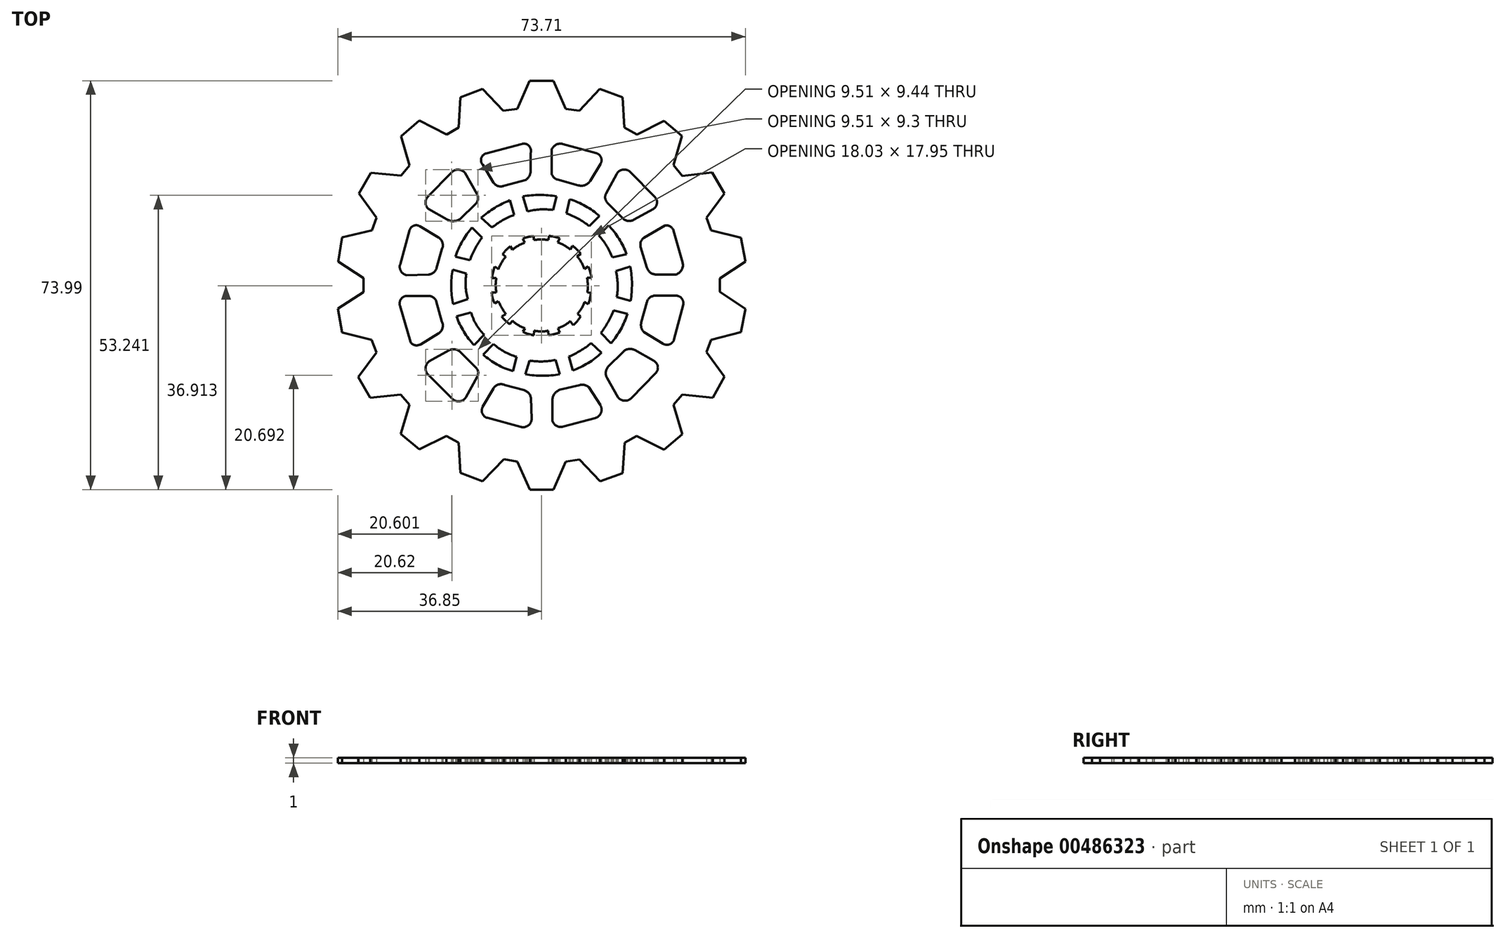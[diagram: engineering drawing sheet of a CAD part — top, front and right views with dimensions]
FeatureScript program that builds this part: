
annotation { "Feature Type Name" : "Feature", "Feature Type Description" : "" }
export const myFeature = defineFeature(function(context is Context, id is Id, definition is map)
    precondition{}
    {
        {
            var Q0;
            Q0=qCreatedBy(makeId("Top.planeOp"),FACE);
            var sketch = newSketch(context, id + "F0", { "sketchPlane" : qUnion([Q0])});
            skLineSegment(sketch, "E0", {"start": v(-17.03, 27.3) * mm, "end": v(-14.85, 28.54) * mm});
            skLineSegment(sketch, "E1", {"start": v(-14.85, 28.54) * mm, "end": v(-14.52, 34.02) * mm});
            skLineSegment(sketch, "E2", {"start": v(-14.52, 34.02) * mm, "end": v(-10.54, 35.55) * mm});
            skLineSegment(sketch, "E3", {"start": v(-10.54, 35.55) * mm, "end": v(-6.75, 31.57) * mm});
            skLineSegment(sketch, "E4", {"start": v(-6.75, 31.57) * mm, "end": v(-4.21, 31.95) * mm});
            skLineSegment(sketch, "E5", {"start": v(-4.21, 31.95) * mm, "end": v(-2.01, 37.02) * mm});
            skLineSegment(sketch, "E6", {"start": v(-2.01, 37.02) * mm, "end": v(2.27, 37.02) * mm});
            skLineSegment(sketch, "E7", {"start": v(2.27, 37.02) * mm, "end": v(4.5, 31.95) * mm});
            skLineSegment(sketch, "E8", {"start": v(4.5, 31.95) * mm, "end": v(7, 31.57) * mm});
            skLineSegment(sketch, "E9", {"start": v(7, 31.57) * mm, "end": v(10.7, 35.55) * mm});
            skLineSegment(sketch, "E10", {"start": v(10.7, 35.55) * mm, "end": v(14.82, 34.02) * mm});
            skLineSegment(sketch, "E11", {"start": v(14.82, 34.02) * mm, "end": v(15.12, 28.54) * mm});
            skLineSegment(sketch, "E12", {"start": v(15.12, 28.54) * mm, "end": v(17.42, 27.3) * mm});
            skLineSegment(sketch, "E13", {"start": v(17.42, 27.3) * mm, "end": v(22.3, 29.76) * mm});
            skLineSegment(sketch, "E14", {"start": v(22.3, 29.76) * mm, "end": v(25.55, 27.03) * mm});
            skLineSegment(sketch, "E15", {"start": v(25.55, 27.03) * mm, "end": v(24.01, 21.74) * mm});
            skLineSegment(sketch, "E16", {"start": v(24.01, 21.74) * mm, "end": v(25.62, 19.8) * mm});
            skLineSegment(sketch, "E17", {"start": v(25.62, 19.8) * mm, "end": v(31.02, 20.4) * mm});
            skLineSegment(sketch, "E18", {"start": v(31.02, 20.4) * mm, "end": v(33.2, 16.62) * mm});
            skLineSegment(sketch, "E19", {"start": v(33.2, 16.62) * mm, "end": v(30.01, 12.24) * mm});
            skLineSegment(sketch, "E20", {"start": v(30.01, 12.24) * mm, "end": v(30.84, 9.94) * mm});
            skLineSegment(sketch, "E21", {"start": v(30.84, 9.94) * mm, "end": v(36.21, 8.6) * mm});
            skLineSegment(sketch, "E22", {"start": v(36.21, 8.6) * mm, "end": v(37.02, 4.26) * mm});
            skLineSegment(sketch, "E23", {"start": v(37.02, 4.26) * mm, "end": v(32.38, 1.27) * mm});
            skLineSegment(sketch, "E24", {"start": v(32.38, 1.27) * mm, "end": v(32.38, -1.18) * mm});
            skLineSegment(sketch, "E25", {"start": v(32.38, -1.18) * mm, "end": v(37.02, -4.3) * mm});
            skLineSegment(sketch, "E26", {"start": v(37.02, -4.3) * mm, "end": v(36.23, -8.5) * mm});
            skLineSegment(sketch, "E27", {"start": v(36.23, -8.5) * mm, "end": v(30.81, -9.85) * mm});
            skLineSegment(sketch, "E28", {"start": v(30.81, -9.85) * mm, "end": v(29.96, -12.09) * mm});
            skLineSegment(sketch, "E29", {"start": v(29.96, -12.09) * mm, "end": v(33.2, -16.56) * mm});
            skLineSegment(sketch, "E30", {"start": v(33.2, -16.56) * mm, "end": v(31.11, -20.31) * mm});
            skLineSegment(sketch, "E31", {"start": v(31.11, -20.31) * mm, "end": v(25.59, -19.74) * mm});
            skLineSegment(sketch, "E32", {"start": v(25.59, -19.74) * mm, "end": v(24.04, -21.63) * mm});
            skLineSegment(sketch, "E33", {"start": v(24.04, -21.63) * mm, "end": v(25.58, -26.96) * mm});
            skLineSegment(sketch, "E34", {"start": v(25.58, -26.96) * mm, "end": v(22.31, -29.71) * mm});
            skLineSegment(sketch, "E35", {"start": v(22.31, -29.71) * mm, "end": v(17.32, -27.25) * mm});
            skLineSegment(sketch, "E36", {"start": v(17.32, -27.25) * mm, "end": v(15.17, -28.48) * mm});
            skLineSegment(sketch, "E37", {"start": v(15.17, -28.48) * mm, "end": v(14.84, -34.01) * mm});
            skLineSegment(sketch, "E38", {"start": v(14.84, -34.01) * mm, "end": v(10.72, -35.46) * mm});
            skLineSegment(sketch, "E39", {"start": v(10.72, -35.46) * mm, "end": v(6.97, -31.5) * mm});
            skLineSegment(sketch, "E40", {"start": v(6.97, -31.5) * mm, "end": v(4.53, -31.92) * mm});
            skLineSegment(sketch, "E41", {"start": v(4.53, -31.92) * mm, "end": v(2.3, -36.97) * mm});
            skLineSegment(sketch, "E42", {"start": v(2.3, -36.97) * mm, "end": v(-1.97, -36.97) * mm});
            skLineSegment(sketch, "E43", {"start": v(-1.97, -36.97) * mm, "end": v(-4.23, -31.92) * mm});
            skLineSegment(sketch, "E44", {"start": v(-4.23, -31.92) * mm, "end": v(-6.66, -31.48) * mm});
            skLineSegment(sketch, "E45", {"start": v(-6.66, -31.48) * mm, "end": v(-10.5, -35.46) * mm});
            skLineSegment(sketch, "E46", {"start": v(-10.5, -35.46) * mm, "end": v(-14.56, -33.92) * mm});
            skLineSegment(sketch, "E47", {"start": v(-14.56, -33.92) * mm, "end": v(-14.87, -28.5) * mm});
            skLineSegment(sketch, "E48", {"start": v(-14.87, -28.5) * mm, "end": v(-17.04, -27.25) * mm});
            skLineSegment(sketch, "E49", {"start": v(-17.04, -27.25) * mm, "end": v(-21.98, -29.68) * mm});
            skLineSegment(sketch, "E50", {"start": v(-21.98, -29.68) * mm, "end": v(-25.3, -26.9) * mm});
            skLineSegment(sketch, "E51", {"start": v(-25.3, -26.9) * mm, "end": v(-23.76, -21.61) * mm});
            skLineSegment(sketch, "E52", {"start": v(-23.76, -21.61) * mm, "end": v(-25.32, -19.78) * mm});
            skLineSegment(sketch, "E53", {"start": v(-25.32, -19.78) * mm, "end": v(-30.85, -20.35) * mm});
            skLineSegment(sketch, "E54", {"start": v(-30.85, -20.35) * mm, "end": v(-33, -16.6) * mm});
            skLineSegment(sketch, "E55", {"start": v(-33, -16.6) * mm, "end": v(-29.73, -12.12) * mm});
            skLineSegment(sketch, "E56", {"start": v(-29.73, -12.12) * mm, "end": v(-30.57, -9.84) * mm});
            skLineSegment(sketch, "E57", {"start": v(-30.57, -9.84) * mm, "end": v(-35.96, -8.52) * mm});
            skLineSegment(sketch, "E58", {"start": v(-35.96, -8.52) * mm, "end": v(-36.7, -4.24) * mm});
            skLineSegment(sketch, "E59", {"start": v(-36.7, -4.24) * mm, "end": v(-32.06, -1.25) * mm});
            skLineSegment(sketch, "E60", {"start": v(-32.06, -1.25) * mm, "end": v(-32.06, 1.28) * mm});
            skLineSegment(sketch, "E61", {"start": v(-32.06, 1.28) * mm, "end": v(-36.66, 4.26) * mm});
            skLineSegment(sketch, "E62", {"start": v(-36.66, 4.26) * mm, "end": v(-35.9, 8.67) * mm});
            skLineSegment(sketch, "E63", {"start": v(-35.9, 8.67) * mm, "end": v(-30.55, 9.94) * mm});
            skLineSegment(sketch, "E64", {"start": v(-30.55, 9.94) * mm, "end": v(-29.69, 12.2) * mm});
            skLineSegment(sketch, "E65", {"start": v(-29.69, 12.2) * mm, "end": v(-32.88, 16.62) * mm});
            skLineSegment(sketch, "E66", {"start": v(-32.88, 16.62) * mm, "end": v(-30.75, 20.39) * mm});
            skLineSegment(sketch, "E67", {"start": v(-30.75, 20.39) * mm, "end": v(-25.28, 19.83) * mm});
            skLineSegment(sketch, "E68", {"start": v(-25.28, 19.83) * mm, "end": v(-23.75, 21.7) * mm});
            skLineSegment(sketch, "E69", {"start": v(-23.75, 21.7) * mm, "end": v(-25.28, 27) * mm});
            skLineSegment(sketch, "E70", {"start": v(-25.28, 27) * mm, "end": v(-21.98, 29.8) * mm});
            skLineSegment(sketch, "E71", {"start": v(-21.98, 29.8) * mm, "end": v(-17.03, 27.3) * mm});
            skLineSegment(sketch, "E72", {"start": v(-21.88, 10.7) * mm, "end": v(-18.54, 8.69) * mm});
            skArc(sketch, "E73", {"start": v(-17.87, 6.53) * mm, "mid": v(-17.79, 7.74) * mm, "end": v(-18.54, 8.69) * mm});
            skLineSegment(sketch, "E74", {"start": v(-17.87, 6.53) * mm, "end": v(-18.83, 3.16) * mm});
            skArc(sketch, "E75", {"start": v(-20.28, 1.94) * mm, "mid": v(-19.37, 2.33) * mm, "end": v(-18.83, 3.16) * mm});
            skLineSegment(sketch, "E76", {"start": v(-20.28, 1.94) * mm, "end": v(-24.3, 1.85) * mm});
            skArc(sketch, "E77", {"start": v(-25.42, 3.86) * mm, "mid": v(-25.3, 2.6) * mm, "end": v(-24.3, 1.85) * mm});
            skLineSegment(sketch, "E78", {"start": v(-25.42, 3.86) * mm, "end": v(-23.73, 9.96) * mm});
            skArc(sketch, "E79", {"start": v(-21.88, 10.7) * mm, "mid": v(-22.99, 10.79) * mm, "end": v(-23.73, 9.96) * mm});
            skLineSegment(sketch, "E80", {"start": v(-24.2, -1.9) * mm, "end": v(-20.36, -1.9) * mm});
            skLineSegment(sketch, "E81", {"start": v(-25.48, -3.7) * mm, "end": v(-23.58, -10.27) * mm});
            skLineSegment(sketch, "E82", {"start": v(-21.73, -10.67) * mm, "end": v(-18.53, -8.75) * mm});
            skLineSegment(sketch, "E83", {"start": v(-18.9, -2.9) * mm, "end": v(-17.87, -6.57) * mm});
            skArc(sketch, "E84", {"start": v(-24.2, -1.9) * mm, "mid": v(-25.28, -2.5) * mm, "end": v(-25.48, -3.7) * mm});
            skArc(sketch, "E85", {"start": v(-23.58, -10.27) * mm, "mid": v(-22.73, -10.84) * mm, "end": v(-21.73, -10.67) * mm});
            skArc(sketch, "E86", {"start": v(-18.53, -8.75) * mm, "mid": v(-17.78, -7.79) * mm, "end": v(-17.87, -6.57) * mm});
            skArc(sketch, "E87", {"start": v(-18.9, -2.9) * mm, "mid": v(-19.47, -2.18) * mm, "end": v(-20.36, -1.9) * mm});
            skLineSegment(sketch, "E88", {"start": v(-14.6, -12.01) * mm, "end": v(-11.87, -14.75) * mm});
            skLineSegment(sketch, "E89", {"start": v(-16.64, -11.78) * mm, "end": v(-20.2, -13.77) * mm});
            skLineSegment(sketch, "E90", {"start": v(-20.34, -16.22) * mm, "end": v(-15.91, -20.58) * mm});
            skLineSegment(sketch, "E91", {"start": v(-11.48, -16.52) * mm, "end": v(-13.5, -20.2) * mm});
            skArc(sketch, "E92", {"start": v(-14.6, -12.01) * mm, "mid": v(-15.59, -11.57) * mm, "end": v(-16.64, -11.78) * mm});
            skArc(sketch, "E93", {"start": v(-20.2, -13.77) * mm, "mid": v(-20.82, -14.96) * mm, "end": v(-20.34, -16.22) * mm});
            skArc(sketch, "E94", {"start": v(-15.91, -20.58) * mm, "mid": v(-14.62, -20.98) * mm, "end": v(-13.5, -20.2) * mm});
            skArc(sketch, "E95", {"start": v(-11.48, -16.52) * mm, "mid": v(-11.35, -15.56) * mm, "end": v(-11.87, -14.75) * mm});
            skLineSegment(sketch, "E96", {"start": v(-6.47, -18.07) * mm, "end": v(-3.03, -18.97) * mm});
            skLineSegment(sketch, "E97", {"start": v(-8.59, -18.69) * mm, "end": v(-10.5, -22.02) * mm});
            skLineSegment(sketch, "E98", {"start": v(-9.66, -24) * mm, "end": v(-3.6, -25.62) * mm});
            skLineSegment(sketch, "E99", {"start": v(-1.78, -20.37) * mm, "end": v(-1.63, -24.2) * mm});
            skArc(sketch, "E100", {"start": v(-6.47, -18.07) * mm, "mid": v(-7.65, -17.95) * mm, "end": v(-8.59, -18.69) * mm});
            skArc(sketch, "E101", {"start": v(-10.5, -22.02) * mm, "mid": v(-10.56, -23.21) * mm, "end": v(-9.66, -24) * mm});
            skArc(sketch, "E102", {"start": v(-3.6, -25.62) * mm, "mid": v(-2.28, -25.38) * mm, "end": v(-1.63, -24.2) * mm});
            skArc(sketch, "E103", {"start": v(-1.78, -20.37) * mm, "mid": v(-2.2, -19.49) * mm, "end": v(-3.03, -18.97) * mm});
            skLineSegment(sketch, "E104", {"start": v(-13.73, 20.35) * mm, "end": v(-11.55, 16.54) * mm});
            skLineSegment(sketch, "E105", {"start": v(-16.13, 20.43) * mm, "end": v(-20.41, 16.05) * mm});
            skLineSegment(sketch, "E106", {"start": v(-11.77, 14.73) * mm, "end": v(-14.57, 11.98) * mm});
            skLineSegment(sketch, "E107", {"start": v(-20.29, 13.8) * mm, "end": v(-16.94, 11.92) * mm});
            skArc(sketch, "E108", {"start": v(-20.41, 16.05) * mm, "mid": v(-20.84, 14.9) * mm, "end": v(-20.29, 13.8) * mm});
            skArc(sketch, "E109", {"start": v(-13.73, 20.35) * mm, "mid": v(-14.91, 20.92) * mm, "end": v(-16.13, 20.43) * mm});
            skArc(sketch, "E110", {"start": v(-11.77, 14.73) * mm, "mid": v(-11.35, 15.6) * mm, "end": v(-11.55, 16.54) * mm});
            skArc(sketch, "E111", {"start": v(-16.94, 11.92) * mm, "mid": v(-15.74, 11.62) * mm, "end": v(-14.57, 11.98) * mm});
            skLineSegment(sketch, "E112", {"start": v(-1.81, 23.97) * mm, "end": v(-1.81, 20.8) * mm});
            skLineSegment(sketch, "E113", {"start": v(-10.48, 21.81) * mm, "end": v(-8.56, 18.61) * mm});
            skLineSegment(sketch, "E114", {"start": v(-2.62, 19.1) * mm, "end": v(-6.64, 18.03) * mm});
            skLineSegment(sketch, "E115", {"start": v(-3.41, 25.6) * mm, "end": v(-9.87, 23.88) * mm});
            skArc(sketch, "E116", {"start": v(-9.87, 23.88) * mm, "mid": v(-10.75, 23.02) * mm, "end": v(-10.48, 21.81) * mm});
            skArc(sketch, "E117", {"start": v(-8.56, 18.61) * mm, "mid": v(-7.71, 17.95) * mm, "end": v(-6.64, 18.03) * mm});
            skArc(sketch, "E118", {"start": v(-2.62, 19.1) * mm, "mid": v(-2.02, 19.86) * mm, "end": v(-1.81, 20.8) * mm});
            skArc(sketch, "E119", {"start": v(-1.81, 23.97) * mm, "mid": v(-2.14, 25.25) * mm, "end": v(-3.41, 25.6) * mm});
            skLineSegment(sketch, "E120", {"start": v(3.47, -18.9) * mm, "end": v(7.07, -18.04) * mm});
            skLineSegment(sketch, "E121", {"start": v(2.08, -20.86) * mm, "end": v(2.08, -24.53) * mm});
            skLineSegment(sketch, "E122", {"start": v(4.06, -25.57) * mm, "end": v(9.88, -24) * mm});
            skLineSegment(sketch, "E123", {"start": v(8.71, -18.42) * mm, "end": v(10.78, -21.7) * mm});
            skArc(sketch, "E124", {"start": v(3.47, -18.9) * mm, "mid": v(2.46, -19.66) * mm, "end": v(2.08, -20.86) * mm});
            skArc(sketch, "E125", {"start": v(8.71, -18.42) * mm, "mid": v(7.94, -18.03) * mm, "end": v(7.07, -18.04) * mm});
            skArc(sketch, "E126", {"start": v(9.88, -24) * mm, "mid": v(10.9, -23.08) * mm, "end": v(10.78, -21.7) * mm});
            skArc(sketch, "E127", {"start": v(2.08, -24.53) * mm, "mid": v(2.86, -25.44) * mm, "end": v(4.06, -25.57) * mm});
            skLineSegment(sketch, "E128", {"start": v(12.15, -14.78) * mm, "end": v(14.85, -12.08) * mm});
            skLineSegment(sketch, "E129", {"start": v(17, -11.73) * mm, "end": v(20.38, -13.62) * mm});
            skLineSegment(sketch, "E130", {"start": v(12, -16.76) * mm, "end": v(14, -20.3) * mm});
            skLineSegment(sketch, "E131", {"start": v(20.79, -15.89) * mm, "end": v(16.4, -20.4) * mm});
            skArc(sketch, "E132", {"start": v(12.15, -14.78) * mm, "mid": v(11.77, -15.75) * mm, "end": v(12, -16.76) * mm});
            skArc(sketch, "E133", {"start": v(17, -11.73) * mm, "mid": v(15.87, -11.53) * mm, "end": v(14.85, -12.08) * mm});
            skArc(sketch, "E134", {"start": v(20.79, -15.89) * mm, "mid": v(21.17, -14.65) * mm, "end": v(20.38, -13.62) * mm});
            skArc(sketch, "E135", {"start": v(14, -20.3) * mm, "mid": v(15.18, -20.88) * mm, "end": v(16.4, -20.4) * mm});
            skLineSegment(sketch, "E136", {"start": v(25.76, -3.47) * mm, "end": v(24.1, -9.9) * mm});
            skLineSegment(sketch, "E137", {"start": v(18.66, -8.44) * mm, "end": v(22.13, -10.56) * mm});
            skLineSegment(sketch, "E138", {"start": v(20.7, -1.87) * mm, "end": v(24.45, -1.87) * mm});
            skLineSegment(sketch, "E139", {"start": v(19.19, -3.06) * mm, "end": v(18.2, -6.7) * mm});
            skArc(sketch, "E140", {"start": v(20.7, -1.87) * mm, "mid": v(19.75, -2.21) * mm, "end": v(19.19, -3.06) * mm});
            skArc(sketch, "E141", {"start": v(25.76, -3.47) * mm, "mid": v(25.49, -2.36) * mm, "end": v(24.45, -1.87) * mm});
            skArc(sketch, "E142", {"start": v(22.13, -10.56) * mm, "mid": v(23.27, -10.7) * mm, "end": v(24.1, -9.9) * mm});
            skArc(sketch, "E143", {"start": v(18.2, -6.7) * mm, "mid": v(18.2, -7.63) * mm, "end": v(18.66, -8.44) * mm});
            skLineSegment(sketch, "E144", {"start": v(18.7, 8.62) * mm, "end": v(22.47, 10.83) * mm});
            skLineSegment(sketch, "E145", {"start": v(24.02, 9.86) * mm, "end": v(25.65, 4.12) * mm});
            skLineSegment(sketch, "E146", {"start": v(20.7, 1.98) * mm, "end": v(24.47, 1.98) * mm});
            skLineSegment(sketch, "E147", {"start": v(18.07, 7) * mm, "end": v(19.22, 3.19) * mm});
            skArc(sketch, "E148", {"start": v(18.7, 8.62) * mm, "mid": v(18.1, 7.91) * mm, "end": v(18.07, 7) * mm});
            skArc(sketch, "E149", {"start": v(24.02, 9.86) * mm, "mid": v(23.43, 10.65) * mm, "end": v(22.47, 10.83) * mm});
            skArc(sketch, "E150", {"start": v(24.47, 1.98) * mm, "mid": v(25.5, 2.8) * mm, "end": v(25.65, 4.12) * mm});
            skArc(sketch, "E151", {"start": v(19.22, 3.19) * mm, "mid": v(19.77, 2.35) * mm, "end": v(20.7, 1.98) * mm});
            skLineSegment(sketch, "E152", {"start": v(16.14, 20.55) * mm, "end": v(20.63, 15.99) * mm});
            skLineSegment(sketch, "E153", {"start": v(13.72, 20.14) * mm, "end": v(11.81, 16.6) * mm});
            skLineSegment(sketch, "E154", {"start": v(20.4, 13.84) * mm, "end": v(16.8, 11.83) * mm});
            skLineSegment(sketch, "E155", {"start": v(12.02, 14.98) * mm, "end": v(15, 12) * mm});
            skArc(sketch, "E156", {"start": v(16.14, 20.55) * mm, "mid": v(14.83, 20.93) * mm, "end": v(13.72, 20.14) * mm});
            skArc(sketch, "E157", {"start": v(11.81, 16.6) * mm, "mid": v(11.66, 15.76) * mm, "end": v(12.02, 14.98) * mm});
            skArc(sketch, "E158", {"start": v(15, 12) * mm, "mid": v(15.87, 11.64) * mm, "end": v(16.8, 11.83) * mm});
            skArc(sketch, "E159", {"start": v(20.4, 13.84) * mm, "mid": v(21.02, 14.86) * mm, "end": v(20.63, 15.99) * mm});
            skLineSegment(sketch, "E160", {"start": v(3.96, 25.57) * mm, "end": v(10.01, 23.9) * mm});
            skLineSegment(sketch, "E161", {"start": v(3.03, 19.13) * mm, "end": v(6.82, 18.1) * mm});
            skLineSegment(sketch, "E162", {"start": v(1.95, 24.43) * mm, "end": v(1.95, 20.28) * mm});
            skLineSegment(sketch, "E163", {"start": v(10.8, 21.97) * mm, "end": v(8.94, 18.9) * mm});
            skArc(sketch, "E164", {"start": v(3.96, 25.57) * mm, "mid": v(2.72, 25.41) * mm, "end": v(1.95, 24.43) * mm});
            skArc(sketch, "E165", {"start": v(10.8, 21.97) * mm, "mid": v(10.9, 23.14) * mm, "end": v(10.01, 23.9) * mm});
            skArc(sketch, "E166", {"start": v(6.82, 18.1) * mm, "mid": v(8.02, 18.13) * mm, "end": v(8.94, 18.9) * mm});
            skArc(sketch, "E167", {"start": v(1.95, 20.28) * mm, "mid": v(2.33, 19.55) * mm, "end": v(3.03, 19.13) * mm});
            skArc(sketch, "E168", {"start": v(2.87, 16.1) * mm, "mid": v(-0.17, 16.36) * mm, "end": v(-3.2, 16.1) * mm});
            skArc(sketch, "E169", {"start": v(2.22, 13.63) * mm, "mid": v(-0.1, 13.74) * mm, "end": v(-2.39, 13.39) * mm});
            skLineSegment(sketch, "E170", {"start": v(-3.2, 16.1) * mm, "end": v(-2.39, 13.39) * mm});
            skLineSegment(sketch, "E171", {"start": v(2.87, 16.1) * mm, "end": v(2.22, 13.63) * mm});
            skArc(sketch, "E172", {"start": v(-5.55, 15.38) * mm, "mid": v(-8.3, 14.04) * mm, "end": v(-10.76, 12.2) * mm});
            skArc(sketch, "E173", {"start": v(-4.8, 12.73) * mm, "mid": v(-6.92, 11.76) * mm, "end": v(-8.82, 10.44) * mm});
            skLineSegment(sketch, "E174", {"start": v(-5.55, 15.38) * mm, "end": v(-4.8, 12.73) * mm});
            skLineSegment(sketch, "E175", {"start": v(-10.76, 12.2) * mm, "end": v(-8.82, 10.44) * mm});
            skArc(sketch, "E176", {"start": v(-12.4, 10.43) * mm, "mid": v(-14.18, 7.98) * mm, "end": v(-15.4, 5.2) * mm});
            skArc(sketch, "E177", {"start": v(-10.62, 8.63) * mm, "mid": v(-11.87, 6.66) * mm, "end": v(-12.82, 4.54) * mm});
            skLineSegment(sketch, "E178", {"start": v(-12.4, 10.43) * mm, "end": v(-10.62, 8.63) * mm});
            skLineSegment(sketch, "E179", {"start": v(-15.4, 5.2) * mm, "end": v(-12.82, 4.54) * mm});
            skArc(sketch, "E180", {"start": v(-15.93, 2.84) * mm, "mid": v(-16.2, -0.27) * mm, "end": v(-15.87, -3.37) * mm});
            skArc(sketch, "E181", {"start": v(-13.46, 2.12) * mm, "mid": v(-13.57, -0.19) * mm, "end": v(-13.22, -2.48) * mm});
            skLineSegment(sketch, "E182", {"start": v(-15.93, 2.84) * mm, "end": v(-13.46, 2.12) * mm});
            skLineSegment(sketch, "E183", {"start": v(-15.87, -3.37) * mm, "end": v(-13.22, -2.48) * mm});
            skArc(sketch, "E184", {"start": v(-12.6, -4.91) * mm, "mid": v(-11.68, -7.07) * mm, "end": v(-10.24, -8.93) * mm});
            skArc(sketch, "E185", {"start": v(-15.26, -5.6) * mm, "mid": v(-13.92, -8.38) * mm, "end": v(-12.04, -10.83) * mm});
            skLineSegment(sketch, "E186", {"start": v(-12.6, -4.91) * mm, "end": v(-15.26, -5.6) * mm});
            skLineSegment(sketch, "E187", {"start": v(-10.24, -8.93) * mm, "end": v(-12.04, -10.83) * mm});
            skArc(sketch, "E188", {"start": v(-10.41, -12.5) * mm, "mid": v(-7.9, -14.33) * mm, "end": v(-5.03, -15.52) * mm});
            skArc(sketch, "E189", {"start": v(-8.55, -10.65) * mm, "mid": v(-6.58, -12) * mm, "end": v(-4.38, -12.93) * mm});
            skLineSegment(sketch, "E190", {"start": v(-8.55, -10.65) * mm, "end": v(-10.41, -12.5) * mm});
            skLineSegment(sketch, "E191", {"start": v(-4.38, -12.93) * mm, "end": v(-5.03, -15.52) * mm});
            skArc(sketch, "E192", {"start": v(-2.05, -13.61) * mm, "mid": v(0.3, -13.78) * mm, "end": v(2.65, -13.48) * mm});
            skArc(sketch, "E193", {"start": v(-2.76, -16.08) * mm, "mid": v(0.33, -16.37) * mm, "end": v(3.42, -16.07) * mm});
            skLineSegment(sketch, "E194", {"start": v(-2.05, -13.61) * mm, "end": v(-2.76, -16.08) * mm});
            skLineSegment(sketch, "E195", {"start": v(2.65, -13.48) * mm, "end": v(3.42, -16.07) * mm});
            skArc(sketch, "E196", {"start": v(5.1, -12.87) * mm, "mid": v(7.21, -11.83) * mm, "end": v(9.12, -10.46) * mm});
            skArc(sketch, "E197", {"start": v(5.8, -15.39) * mm, "mid": v(8.56, -14.07) * mm, "end": v(10.98, -12.19) * mm});
            skLineSegment(sketch, "E198", {"start": v(9.12, -10.46) * mm, "end": v(10.98, -12.19) * mm});
            skLineSegment(sketch, "E199", {"start": v(5.1, -12.87) * mm, "end": v(5.8, -15.39) * mm});
            skArc(sketch, "E200", {"start": v(12.74, -10.47) * mm, "mid": v(14.47, -7.96) * mm, "end": v(15.67, -5.15) * mm});
            skArc(sketch, "E201", {"start": v(10.87, -8.6) * mm, "mid": v(12.2, -6.66) * mm, "end": v(13.18, -4.52) * mm});
            skLineSegment(sketch, "E202", {"start": v(13.18, -4.52) * mm, "end": v(15.67, -5.15) * mm});
            skLineSegment(sketch, "E203", {"start": v(10.87, -8.6) * mm, "end": v(12.74, -10.47) * mm});
            skArc(sketch, "E204", {"start": v(16.25, -2.8) * mm, "mid": v(16.5, 0.29) * mm, "end": v(16.2, 3.38) * mm});
            skArc(sketch, "E205", {"start": v(13.75, -2.14) * mm, "mid": v(13.91, 0.23) * mm, "end": v(13.62, 2.6) * mm});
            skLineSegment(sketch, "E206", {"start": v(16.2, 3.38) * mm, "end": v(13.62, 2.6) * mm});
            skLineSegment(sketch, "E207", {"start": v(13.75, -2.14) * mm, "end": v(16.25, -2.8) * mm});
            skArc(sketch, "E208", {"start": v(15.54, 5.66) * mm, "mid": v(14.15, 8.41) * mm, "end": v(12.3, 10.87) * mm});
            skArc(sketch, "E209", {"start": v(12.93, 5.03) * mm, "mid": v(11.91, 7.15) * mm, "end": v(10.5, 9.03) * mm});
            skLineSegment(sketch, "E210", {"start": v(12.3, 10.87) * mm, "end": v(10.5, 9.03) * mm});
            skLineSegment(sketch, "E211", {"start": v(15.54, 5.66) * mm, "end": v(12.93, 5.03) * mm});
            skArc(sketch, "E212", {"start": v(10.6, 12.54) * mm, "mid": v(8.08, 14.36) * mm, "end": v(5.22, 15.57) * mm});
            skArc(sketch, "E213", {"start": v(8.77, 10.7) * mm, "mid": v(6.81, 12.04) * mm, "end": v(4.64, 13) * mm});
            skLineSegment(sketch, "E214", {"start": v(5.22, 15.57) * mm, "end": v(4.64, 13) * mm});
            skLineSegment(sketch, "E215", {"start": v(10.6, 12.54) * mm, "end": v(8.77, 10.7) * mm});
            skArc(sketch, "E216", {"start": v(-3.21, -8.43) * mm, "mid": v(-2.27, -8.81) * mm, "end": v(-1.28, -9.03) * mm});
            skArc(sketch, "E217", {"start": v(-1.22, -8.19) * mm, "mid": v(0.07, -8.35) * mm, "end": v(1.35, -8.2) * mm});
            skArc(sketch, "E218", {"start": v(3.1, -7.75) * mm, "mid": v(4.29, -7.23) * mm, "end": v(5.34, -6.48) * mm});
            skArc(sketch, "E219", {"start": v(6.66, -5.16) * mm, "mid": v(7.4, -4.14) * mm, "end": v(7.92, -2.98) * mm});
            skArc(sketch, "E220", {"start": v(8.45, -1.27) * mm, "mid": v(8.52, 0.07) * mm, "end": v(8.37, 1.4) * mm});
            skArc(sketch, "E221", {"start": v(-5.13, -6.42) * mm, "mid": v(-4.06, -7.2) * mm, "end": v(-2.86, -7.75) * mm});
            skArc(sketch, "E222", {"start": v(-7.66, -2.9) * mm, "mid": v(-7.05, -4.08) * mm, "end": v(-6.34, -5.2) * mm});
            skArc(sketch, "E223", {"start": v(-8.03, 1.34) * mm, "mid": v(-8.15, 0.02) * mm, "end": v(-8.03, -1.3) * mm});
            skArc(sketch, "E224", {"start": v(-6.32, 5.2) * mm, "mid": v(-7.09, 4.12) * mm, "end": v(-7.64, 2.9) * mm});
            skArc(sketch, "E225", {"start": v(-2.88, 7.73) * mm, "mid": v(-4.07, 7.18) * mm, "end": v(-5.15, 6.44) * mm});
            skArc(sketch, "E226", {"start": v(1.4, 8.2) * mm, "mid": v(0.08, 8.29) * mm, "end": v(-1.24, 8.2) * mm});
            skArc(sketch, "E227", {"start": v(5.32, 6.48) * mm, "mid": v(4.24, 7.24) * mm, "end": v(3.04, 7.8) * mm});
            skArc(sketch, "E228", {"start": v(7.92, 2.98) * mm, "mid": v(7.33, 4.17) * mm, "end": v(6.58, 5.27) * mm});
            skArc(sketch, "E229", {"start": v(7.24, 5.72) * mm, "mid": v(6.53, 6.48) * mm, "end": v(5.74, 7.16) * mm});
            skArc(sketch, "E230", {"start": v(3.45, 8.47) * mm, "mid": v(2.48, 8.8) * mm, "end": v(1.47, 8.92) * mm});
            skArc(sketch, "E231", {"start": v(-1.25, 8.9) * mm, "mid": v(-2.26, 8.76) * mm, "end": v(-3.23, 8.45) * mm});
            skArc(sketch, "E232", {"start": v(-5.5, 7.08) * mm, "mid": v(-6.25, 6.4) * mm, "end": v(-6.9, 5.61) * mm});
            skArc(sketch, "E233", {"start": v(-8.32, 3.39) * mm, "mid": v(-8.62, 2.37) * mm, "end": v(-8.8, 1.33) * mm});
            skArc(sketch, "E234", {"start": v(-8.85, -1.29) * mm, "mid": v(-8.7, -2.32) * mm, "end": v(-8.32, -3.3) * mm});
            skArc(sketch, "E235", {"start": v(-7.04, -5.64) * mm, "mid": v(-6.4, -6.4) * mm, "end": v(-5.6, -7) * mm});
            skArc(sketch, "E236", {"start": v(1.4, -9.02) * mm, "mid": v(2.43, -8.85) * mm, "end": v(3.43, -8.53) * mm});
            skArc(sketch, "E237", {"start": v(5.82, -7.23) * mm, "mid": v(6.6, -6.5) * mm, "end": v(7.17, -5.61) * mm});
            skArc(sketch, "E238", {"start": v(8.61, -3.36) * mm, "mid": v(8.9, -2.38) * mm, "end": v(9.08, -1.36) * mm});
            skArc(sketch, "E239", {"start": v(9.17, 1.4) * mm, "mid": v(8.96, 2.41) * mm, "end": v(8.61, 3.39) * mm});
            skLineSegment(sketch, "E240", {"start": v(-1.25, 8.9) * mm, "end": v(-1.24, 8.2) * mm});
            skLineSegment(sketch, "E241", {"start": v(1.47, 8.92) * mm, "end": v(1.4, 8.2) * mm});
            skLineSegment(sketch, "E242", {"start": v(3.45, 8.47) * mm, "end": v(3.04, 7.8) * mm});
            skLineSegment(sketch, "E243", {"start": v(5.74, 7.16) * mm, "end": v(5.32, 6.48) * mm});
            skLineSegment(sketch, "E244", {"start": v(7.24, 5.72) * mm, "end": v(6.58, 5.27) * mm});
            skLineSegment(sketch, "E245", {"start": v(8.61, 3.39) * mm, "end": v(7.92, 2.98) * mm});
            skLineSegment(sketch, "E246", {"start": v(9.17, 1.4) * mm, "end": v(8.37, 1.4) * mm});
            skLineSegment(sketch, "E247", {"start": v(9.08, -1.36) * mm, "end": v(8.45, -1.27) * mm});
            skLineSegment(sketch, "E248", {"start": v(7.92, -2.98) * mm, "end": v(8.61, -3.36) * mm});
            skLineSegment(sketch, "E249", {"start": v(6.66, -5.16) * mm, "end": v(7.17, -5.61) * mm});
            skLineSegment(sketch, "E250", {"start": v(5.34, -6.48) * mm, "end": v(5.82, -7.23) * mm});
            skLineSegment(sketch, "E251", {"start": v(3.1, -7.75) * mm, "end": v(3.43, -8.53) * mm});
            skLineSegment(sketch, "E252", {"start": v(1.35, -8.2) * mm, "end": v(1.4, -9.02) * mm});
            skLineSegment(sketch, "E253", {"start": v(-1.22, -8.19) * mm, "end": v(-1.28, -9.03) * mm});
            skLineSegment(sketch, "E254", {"start": v(-2.86, -7.75) * mm, "end": v(-3.21, -8.43) * mm});
            skLineSegment(sketch, "E255", {"start": v(-5.13, -6.42) * mm, "end": v(-5.6, -7) * mm});
            skLineSegment(sketch, "E256", {"start": v(-6.34, -5.2) * mm, "end": v(-7.04, -5.64) * mm});
            skLineSegment(sketch, "E257", {"start": v(-7.66, -2.9) * mm, "end": v(-8.32, -3.3) * mm});
            skLineSegment(sketch, "E258", {"start": v(-8.03, -1.3) * mm, "end": v(-8.85, -1.29) * mm});
            skLineSegment(sketch, "E259", {"start": v(-8.03, 1.34) * mm, "end": v(-8.8, 1.33) * mm});
            skLineSegment(sketch, "E260", {"start": v(-7.64, 2.9) * mm, "end": v(-8.32, 3.39) * mm});
            skLineSegment(sketch, "E261", {"start": v(-6.32, 5.2) * mm, "end": v(-6.9, 5.61) * mm});
            skLineSegment(sketch, "E262", {"start": v(-5.5, 7.08) * mm, "end": v(-5.15, 6.44) * mm});
            skLineSegment(sketch, "E263", {"start": v(-3.23, 8.45) * mm, "end": v(-2.88, 7.73) * mm});
            skSolve(sketch);
        }
        {
            var Q0;
            Q0 = qSketchRegion(id + "F0", true);
            extrude(context, id + "F1", {"entities" : qUnion([Q0]), "depth" : 1 * mm, "offsetDistance" : 25 * mm});
        }
    });
